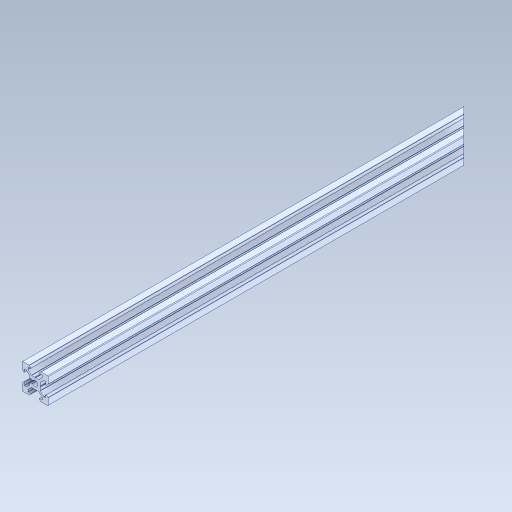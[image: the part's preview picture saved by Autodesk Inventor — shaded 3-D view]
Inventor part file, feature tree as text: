
AUTODESK INVENTOR PART (.ipt)
format: ipt  version: 2023 (Build 270158000, 158)  size: 425,984 bytes
history: mixed  units: in
note: dims shown in document units (in); Inventor stores cm internally (conversion verified against a paired STEP export)
features: other x3, extrude x2, sketch x2, projected_geometry x1, imported_body x1
ambient origin geometry x8: Origin, YZ Plane, XZ Plane, XY Plane, X Axis, Y Axis, Z Axis, Center Point
bodies: Solid1 (imported_parasolid)
feature tree (9):
  other  "Annotations"
  other  "Boss-Extrude1"
  extrude  "Extrusion1"  Depth=12.5984in
  extrude  "Extrusion2"  TaperAngle=0.0deg  [1 undecoded]
  sketch  "Sketch2"  dims[d5=3.0748in d6=0.0in d7=12.5984in]
  projected_geometry  "Projected Loop1"
  sketch  "Sketch3"  dims[d9=45.0deg d10=0.0in d11=0.0in d0=0.106in d1=0.114in d2=17.3228in]
  other  "Linear Dimension 1"
  imported_body  NMx_Import_Brep_tag  [imported B-rep: ~114 faces, bbox_mm=[20.0, 20.0, 339.912132]]
note: 1 required parameter value undecoded (feature->parameter linkage not recoverable at this tier; creation-order binding heuristic only, values carry confidence <= 0.55)
